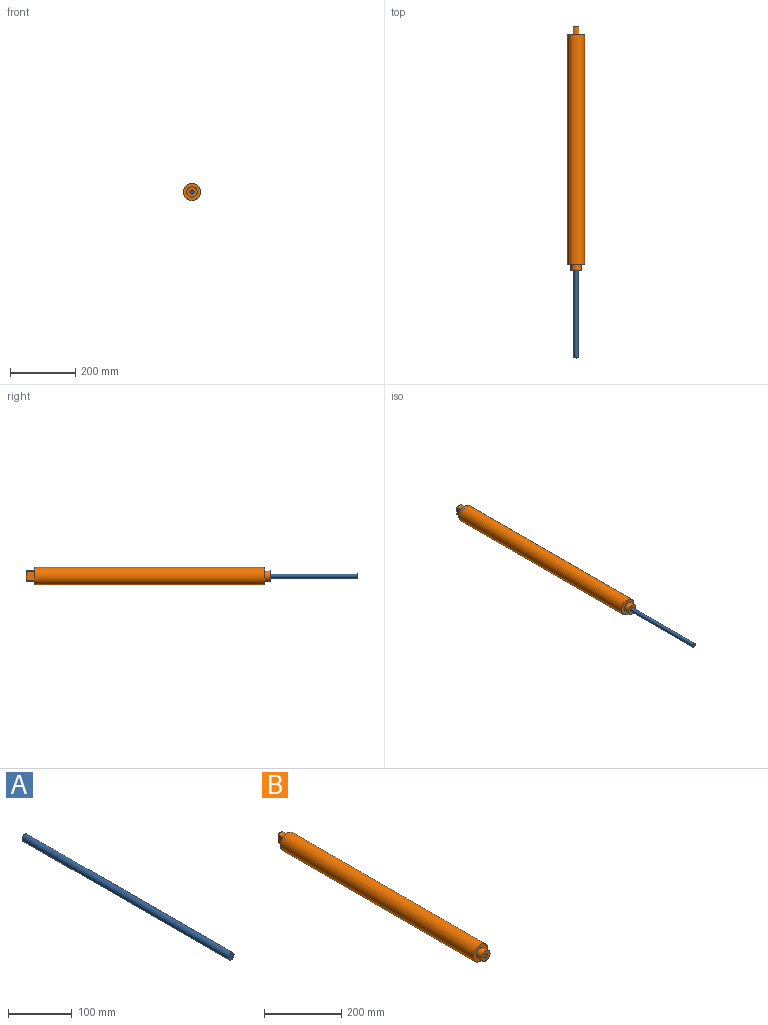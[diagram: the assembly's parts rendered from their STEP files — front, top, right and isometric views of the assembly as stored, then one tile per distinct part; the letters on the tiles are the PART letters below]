
ASSEMBLY  parts=2 mates=1
PART A: 3 faces, bbox 12.7x457.2x12.7 mm
  f0: cylinder r=6.35mm len=457.2mm, axis (0,1,0), area 18241.5mm2, adj f1,f2
  f1: plane 12.7x12.7mm, normal (0,-1,0), area 126.7mm2, adj f0
  f2: plane 12.7x12.7mm, normal (0,1,0), area 126.7mm2, adj f0
PART B: 14 faces, bbox 52.7x752.2x52.7 mm
  f0: plane 52.71x52.71mm, normal (0,1,0), area 1637.5mm2, adj f1,f9,f10,f11,f12
  f1: cylinder r=26.35mm len=708.03mm, axis (0,-1,0), area 117233.1mm2, adj f0,f2
  f2: plane 52.71x52.71mm, normal (0,-1,0), area 1396.3mm2, adj f1,f3
  f3: cylinder r=15.81mm len=31.62mm, axis (0,-1,0), area 1879.9mm2, adj f2,f4
  f4: plane 31.62x31.62mm, normal (0,-1,0), area 658.7mm2, adj f3,f5
  f5: cylinder r=6.35mm len=25.27mm, axis (0,-1,0), area 1008.3mm2, adj f4,f6
  f6: plane 48.26x48.26mm, normal (0,1,0), area 1702.5mm2, adj f5,f7
  f7: cylinder r=24.13mm len=695.33mm, axis (0,-1,0), area 105420.5mm2, adj f6,f8
  f8: plane 48.26x48.26mm, normal (0,-1,0), area 1829.2mm2, adj f7
  f9: plane 25.8x25.27mm, normal (-1,0,0), area 652mm2, adj f0,f10,f12,f13
  f10: cylinder r=15.81mm len=25.27mm, axis (0,-1,0), area 492.8mm2, adj f0,f9,f11,f13
  f11: plane 25.8x25.27mm, normal (1,0,0), area 652mm2, adj f0,f10,f12,f13
  f12: cylinder r=15.81mm len=25.27mm, axis (0,-1,0), area 492.8mm2, adj f0,f9,f11,f13
  f13: plane 31.62x18.29mm, normal (0,1,0), area 544.2mm2, adj f9,f10,f11,f12
PLACE A t=(27.96,-381.72,-119.05)mm
PLACE B t=(27.96,155.39,-119.05)mm
MATE cylindrical A.f0 <-> B.f1  axis (0,1,0) through (27.96,-381.72,-119.05)mm
